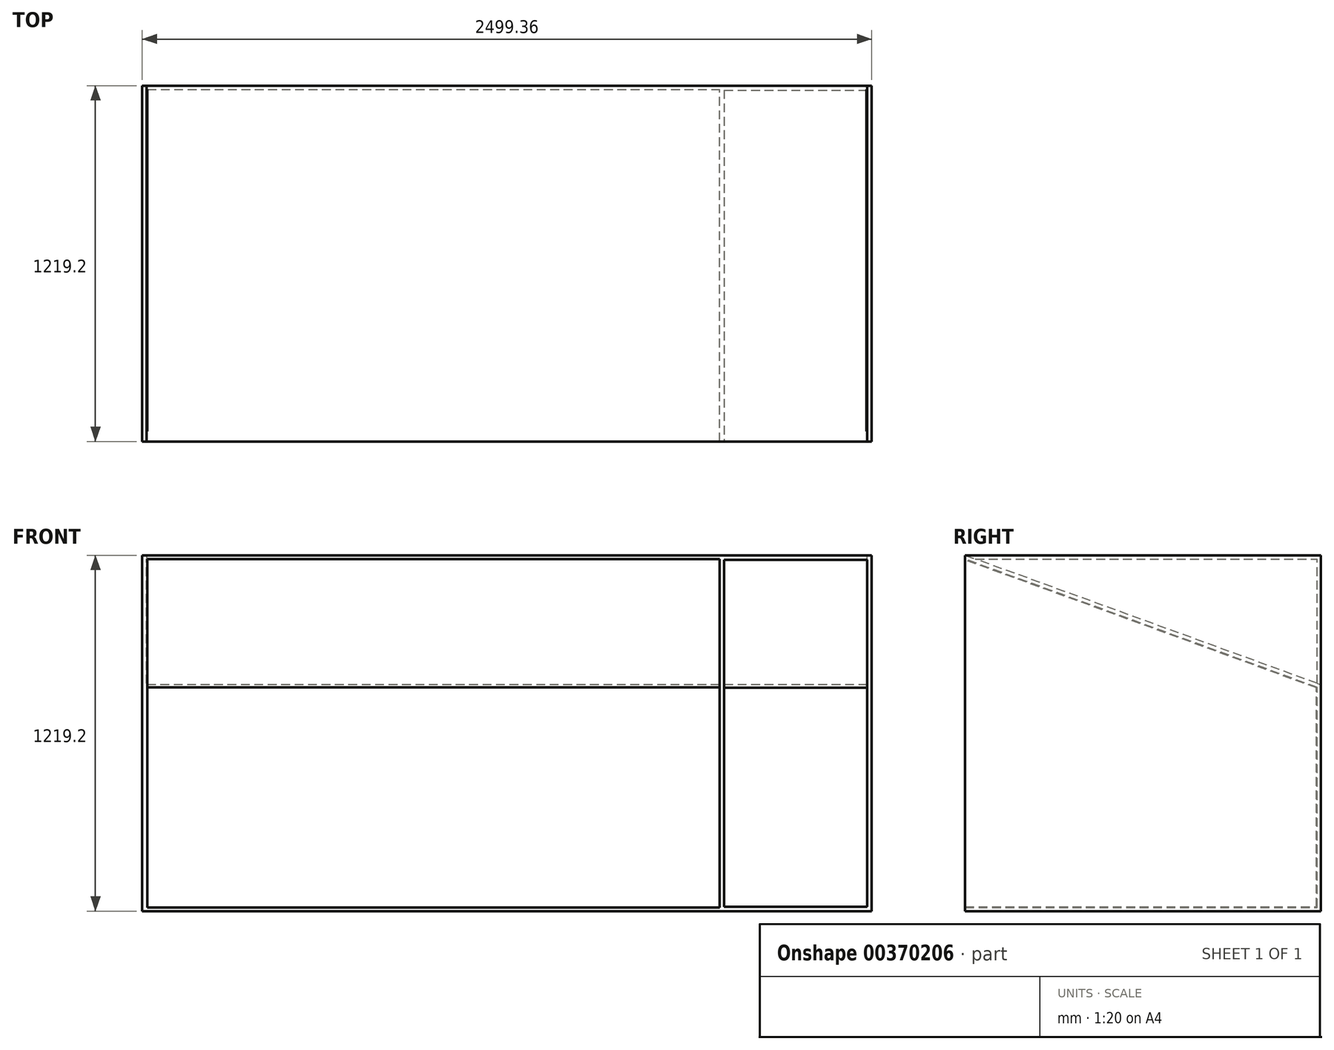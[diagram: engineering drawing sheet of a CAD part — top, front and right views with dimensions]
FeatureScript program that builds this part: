
annotation { "Feature Type Name" : "Feature", "Feature Type Description" : "" }
export const myFeature = defineFeature(function(context is Context, id is Id, definition is map)
    precondition{}
    {
        {
            var Q0;
            Q0=qCreatedBy(makeId("Top.planeOp"),FACE);
            var sketch = newSketch(context, id + "F0", { "sketchPlane" : qUnion([Q0])});
            skLineSegment(sketch, "E0.bottom", {"start": v(-1219.2, 702.71) * mm, "end": v(1219.2, 702.71) * mm});
            skLineSegment(sketch, "E0.top", {"start": v(-1219.2, -516.49) * mm, "end": v(1219.2, -516.49) * mm});
            skLineSegment(sketch, "E0.left", {"start": v(-1219.2, 702.71) * mm, "end": v(-1219.2, -516.49) * mm});
            skLineSegment(sketch, "E0.right", {"start": v(1219.2, 702.71) * mm, "end": v(1219.2, -516.49) * mm});
            skSolve(sketch);
        }
        {
            var Q0;
            Q0 = qSketchRegion(id + "F0", true);
            extrude(context, id + "F1", {"entities" : qUnion([Q0]), "depth" : 1219.2 * mm});
        }
        {
            var Q0;
            Q0=makeQuery(id+"F1.opExtrude","SWEPT_FACE",FACE,{"disambiguationData":[OSD([sQuery(id+"F0.wireOp",EDGE,"E0.left")])]});
            var sketch = newSketch(context, id + "F2", { "sketchPlane" : qUnion([Q0])});
            skLineSegment(sketch, "E1", {"start": v(516.49, 1219.2) * mm, "end": v(-702.71, 775.45) * mm});
            skSolve(sketch);
        }
        {
            var Q0;
            {var subQ0=sQuery(id+"F2.wireOp",EDGE,"E1");Q0=makeQuery(id+"F2.imprint","IMPRINT",FACE,{"disambiguationData":[TD([[makeQuery(id+"F2.imprint","IMPRINT",EDGE,{"derivedFrom":subQ0}),-1.0]])]});}
            extrude(context, id + "F3", {"entities" : qUnion([Q0]), "operationType" : NewBodyOperationType.REMOVE, "endBound" : BoundingType.THROUGH_ALL, "oppositeDirection" : true, "depth" : 30.48 * mm});
        }
        {
            var Q0;
            Q0=makeQuery(id+"F1.opExtrude","SWEPT_FACE",FACE,{"disambiguationData":[OSD([sQuery(id+"F0.wireOp",EDGE,"E0.right")])]});
            var sketch = newSketch(context, id + "F4", { "sketchPlane" : qUnion([Q0])});
            skLineSegment(sketch, "E2.bottom", {"start": v(-516.49, 1219.2) * mm, "end": v(702.71, 1219.2) * mm});
            skLineSegment(sketch, "E2.top", {"start": v(-516.49, 0) * mm, "end": v(702.71, 0) * mm});
            skLineSegment(sketch, "E2.left", {"start": v(-516.49, 1219.2) * mm, "end": v(-516.49, 0) * mm});
            skLineSegment(sketch, "E2.right", {"start": v(702.71, 1219.2) * mm, "end": v(702.71, 0) * mm});
            skSolve(sketch);
        }
        {
            var Q0;
            {var subQ0=sQuery(id+"F4.wireOp",EDGE,"E2.bottom");Q0=makeQuery(id+"F4.imprint","IMPRINT",FACE,{"disambiguationData":[TD([[makeQuery(id+"F4.imprint","IMPRINT",EDGE,{"derivedFrom":subQ0}),-1.0]])]});}
            var Q1;
            {var subQ0=sQuery(id+"F4.wireOp",EDGE,"E2.top");Q1=makeQuery(id+"F4.imprint","IMPRINT",FACE,{"disambiguationData":[TD([[makeQuery(id+"F4.imprint","IMPRINT",EDGE,{"derivedFrom":subQ0}),-1.0]])]});}
            extrude(context, id + "F5", {"entities" : qUnion([Q0, Q1]), "operationType" : NewBodyOperationType.ADD, "depth" : 30.48 * mm});
        }
        {
            var Q0;
            Q0=makeQuery(id+"F1.opExtrude","SWEPT_FACE",FACE,{"disambiguationData":[OSD([sQuery(id+"F0.wireOp",EDGE,"E0.left")])]});
            var sketch = newSketch(context, id + "F6", { "sketchPlane" : qUnion([Q0])});
            skLineSegment(sketch, "E3.bottom", {"start": v(516.49, 1219.2) * mm, "end": v(-702.71, 1219.2) * mm});
            skLineSegment(sketch, "E3.top", {"start": v(516.49, 0) * mm, "end": v(-702.71, 0) * mm});
            skLineSegment(sketch, "E3.left", {"start": v(516.49, 1219.2) * mm, "end": v(516.49, 0) * mm});
            skLineSegment(sketch, "E3.right", {"start": v(-702.71, 1219.2) * mm, "end": v(-702.71, 0) * mm});
            skSolve(sketch);
        }
        {
            var Q0;
            {var subQ0=sQuery(id+"F6.wireOp",EDGE,"E3.top");Q0=makeQuery(id+"F6.imprint","IMPRINT",FACE,{"disambiguationData":[TD([[makeQuery(id+"F6.imprint","IMPRINT",EDGE,{"derivedFrom":subQ0}),1.0]])]});}
            var Q1;
            {var subQ0=sQuery(id+"F6.wireOp",EDGE,"E3.bottom");Q1=makeQuery(id+"F6.imprint","IMPRINT",FACE,{"disambiguationData":[TD([[makeQuery(id+"F6.imprint","IMPRINT",EDGE,{"derivedFrom":subQ0}),1.0]])]});}
            extrude(context, id + "F7", {"entities" : qUnion([Q0, Q1]), "operationType" : NewBodyOperationType.ADD, "depth" : 30.48 * mm});
        }
        {
            var Q0;
            Q0=makeQuery(id+"F5.boolean.opBoolean","MERGE",FACE,{"derivedFrom":[makeQuery(id+"F1.opExtrude","SWEPT_FACE",FACE,{"disambiguationData":[OSD([sQuery(id+"F0.wireOp",EDGE,"E0.top")])]}),makeQuery(id+"F5.opExtrude","SWEPT_FACE",FACE,{"disambiguationData":[OSD([sQuery(id+"F4.wireOp",EDGE,"E2.left")])]})]});
            shell(context, id + "F8", {"entities" : qUnion([Q0]), "thickness" : 12.7 * mm});
        }
        {
            var Q0;
            Q0=makeQuery(id+"F7.opExtrude","CAP_FACE",FACE,{"disambiguationData":[OSD([sQuery(id+"F6.wireOp",EDGE,"E3.bottom"),sQuery(id+"F6.wireOp",EDGE,"E3.top"),sQuery(id+"F6.wireOp",EDGE,"E3.left"),sQuery(id+"F6.wireOp",EDGE,"E3.right")])],"isStart":true});
            extrude(context, id + "F9", {"entities" : qUnion([Q0]), "operationType" : NewBodyOperationType.REMOVE, "oppositeDirection" : true, "depth" : 15.24 * mm});
        }
        {
            var Q0;
            Q0=makeQuery(id+"F5.opExtrude","CAP_FACE",FACE,{"disambiguationData":[OSD([sQuery(id+"F4.wireOp",EDGE,"E2.bottom"),sQuery(id+"F4.wireOp",EDGE,"E2.top"),sQuery(id+"F4.wireOp",EDGE,"E2.left"),sQuery(id+"F4.wireOp",EDGE,"E2.right")])],"isStart":true});
            extrude(context, id + "F10", {"entities" : qUnion([Q0]), "operationType" : NewBodyOperationType.REMOVE, "oppositeDirection" : true, "depth" : 15.24 * mm});
        }
        {
            var Q0;
            {var subQ0=sQuery(id+"F6.wireOp",EDGE,"E3.right");var subQ1=sQuery(id+"F6.wireOp",EDGE,"E3.left");var subQ2=sQuery(id+"F6.wireOp",EDGE,"E3.top");var subQ3=sQuery(id+"F6.wireOp",EDGE,"E3.bottom");Q0=makeQuery(id+"F8.opShell","OFFSET_FACE",FACE,{"disambiguationData":[OSD([subQ3,subQ2,subQ1,subQ0]),TDD([makeQuery(id+"F7.opExtrude","CAP_FACE",FACE,{"disambiguationData":[OSD([subQ3,subQ2,subQ1,subQ0])],"isStart":false})])]});}
            var Q1;
            {var subQ0=sQuery(id+"F6.wireOp",EDGE,"E3.right");var subQ1=sQuery(id+"F6.wireOp",EDGE,"E3.left");var subQ2=sQuery(id+"F6.wireOp",EDGE,"E3.top");var subQ3=sQuery(id+"F6.wireOp",EDGE,"E3.bottom");Q1=makeQuery(id+"F8.opShell","OFFSET_FACE",FACE,{"disambiguationData":[OSD([subQ3,subQ2,subQ1,subQ0]),TDD([makeQuery(id+"F7.opExtrude","CAP_FACE",FACE,{"disambiguationData":[OSD([subQ3,subQ2,subQ1,subQ0])],"isStart":true})])]});}
            extrude(context, id + "F11", {"entities" : qUnion([Q0]), "operationType" : NewBodyOperationType.ADD, "endBound" : BoundingType.UP_TO_SURFACE, "endBoundEntityFace" : qUnion([Q1]), "depth" : 30.48 * mm});
        }
        {
            var Q0;
            {var subQ0=sQuery(id+"F4.wireOp",EDGE,"E2.right");var subQ1=sQuery(id+"F4.wireOp",EDGE,"E2.left");var subQ2=sQuery(id+"F4.wireOp",EDGE,"E2.top");var subQ3=sQuery(id+"F4.wireOp",EDGE,"E2.bottom");Q0=makeQuery(id+"F8.opShell","OFFSET_FACE",FACE,{"disambiguationData":[OSD([subQ3,subQ2,subQ1,subQ0]),TDD([makeQuery(id+"F5.opExtrude","CAP_FACE",FACE,{"disambiguationData":[OSD([subQ3,subQ2,subQ1,subQ0])],"isStart":false})])]});}
            var Q1;
            {var subQ0=sQuery(id+"F4.wireOp",EDGE,"E2.right");var subQ1=sQuery(id+"F4.wireOp",EDGE,"E2.left");var subQ2=sQuery(id+"F4.wireOp",EDGE,"E2.top");var subQ3=sQuery(id+"F4.wireOp",EDGE,"E2.bottom");Q1=makeQuery(id+"F8.opShell","OFFSET_FACE",FACE,{"disambiguationData":[OSD([subQ3,subQ2,subQ1,subQ0]),TDD([makeQuery(id+"F5.opExtrude","CAP_FACE",FACE,{"disambiguationData":[OSD([subQ3,subQ2,subQ1,subQ0])],"isStart":true})])]});}
            extrude(context, id + "F12", {"entities" : qUnion([Q0]), "operationType" : NewBodyOperationType.ADD, "endBound" : BoundingType.UP_TO_SURFACE, "endBoundEntityFace" : qUnion([Q1]), "depth" : 30.48 * mm});
        }
        {
            var Q0;
            {var subQ1=sQuery(id+"F4.wireOp",EDGE,"E2.right");var subQ3=sQuery(id+"F4.wireOp",EDGE,"E2.left");var subQ4=sQuery(id+"F0.wireOp",EDGE,"E0.top");var subQ5=sQuery(id+"F4.wireOp",EDGE,"E2.top");Q0=makeQuery(id+"F12.boolean.opBoolean","SPLIT",FACE,{"disambiguationData":[TD([makeQuery(id+"F1.opExtrude","SWEPT_FACE",FACE,{"disambiguationData":[OSD([subQ4])]})])],"derivedFrom":makeQuery(id+"F12.opExtrude","CAP_FACE",FACE,{"disambiguationData":[OSD([sQuery(id+"F4.wireOp",EDGE,"E2.bottom"),subQ5,subQ3,subQ1])],"isStart":false})});}
            extrude(context, id + "F13", {"entities" : qUnion([Q0]), "operationType" : NewBodyOperationType.ADD, "depth" : 502.92 * mm});
        }
        {
            var Q0;
            {var subQ0=sQuery(id+"F4.wireOp",EDGE,"E2.right");var subQ1=sQuery(id+"F4.wireOp",EDGE,"E2.left");var subQ2=sQuery(id+"F4.wireOp",EDGE,"E2.top");var subQ3=sQuery(id+"F4.wireOp",EDGE,"E2.bottom");var subQ4=sQuery(id+"F6.wireOp",EDGE,"E3.left");Q0=makeQuery(id+"F13.boolean.opBoolean","MERGE",FACE,{"derivedFrom":[makeQuery(id+"F12.boolean.opBoolean","MERGE",FACE,{"derivedFrom":[makeQuery(id+"F11.boolean.opBoolean","MERGE",FACE,{"derivedFrom":[makeQuery(id+"F7.boolean.opBoolean","MERGE",FACE,{"derivedFrom":[makeQuery(id+"F5.boolean.opBoolean","MERGE",FACE,{"derivedFrom":[makeQuery(id+"F1.opExtrude","SWEPT_FACE",FACE,{"disambiguationData":[OSD([sQuery(id+"F0.wireOp",EDGE,"E0.top")])]}),makeQuery(id+"F5.opExtrude","SWEPT_FACE",FACE,{"disambiguationData":[OSD([subQ1])]})]}),makeQuery(id+"F7.opExtrude","SWEPT_FACE",FACE,{"disambiguationData":[OSD([subQ4])]})]}),makeQuery(id+"F11.opExtrude","SWEPT_FACE",FACE,{"disambiguationData":[OSD([subQ4])]})]}),makeQuery(id+"F12.opExtrude","SWEPT_FACE",FACE,{"disambiguationData":[OSD([subQ1])]})]}),makeQuery(id+"F13.opExtrude","SWEPT_FACE",FACE,{"disambiguationData":[OSD([subQ3,subQ2,subQ1,subQ0]),TDD([makeQuery(id+"F12.opExtrude","TWEAK_EDGE",EDGE,{"derivedFrom":[makeQuery(id+"F8.opShell","OFFSET_EDGE",EDGE,{"disambiguationData":[OSD([subQ1])]}),makeQuery(id+"F8.opShell","OFFSET_FACE",FACE,{"disambiguationData":[OSD([subQ3,subQ2,subQ1,subQ0]),TDD([makeQuery(id+"F5.opExtrude","CAP_FACE",FACE,{"disambiguationData":[OSD([subQ3,subQ2,subQ1,subQ0])],"isStart":true})])]})]})])]})]});}
            shell(context, id + "F14", {"entities" : qUnion([Q0]), "thickness" : 15.24 * mm});
        }
    });
